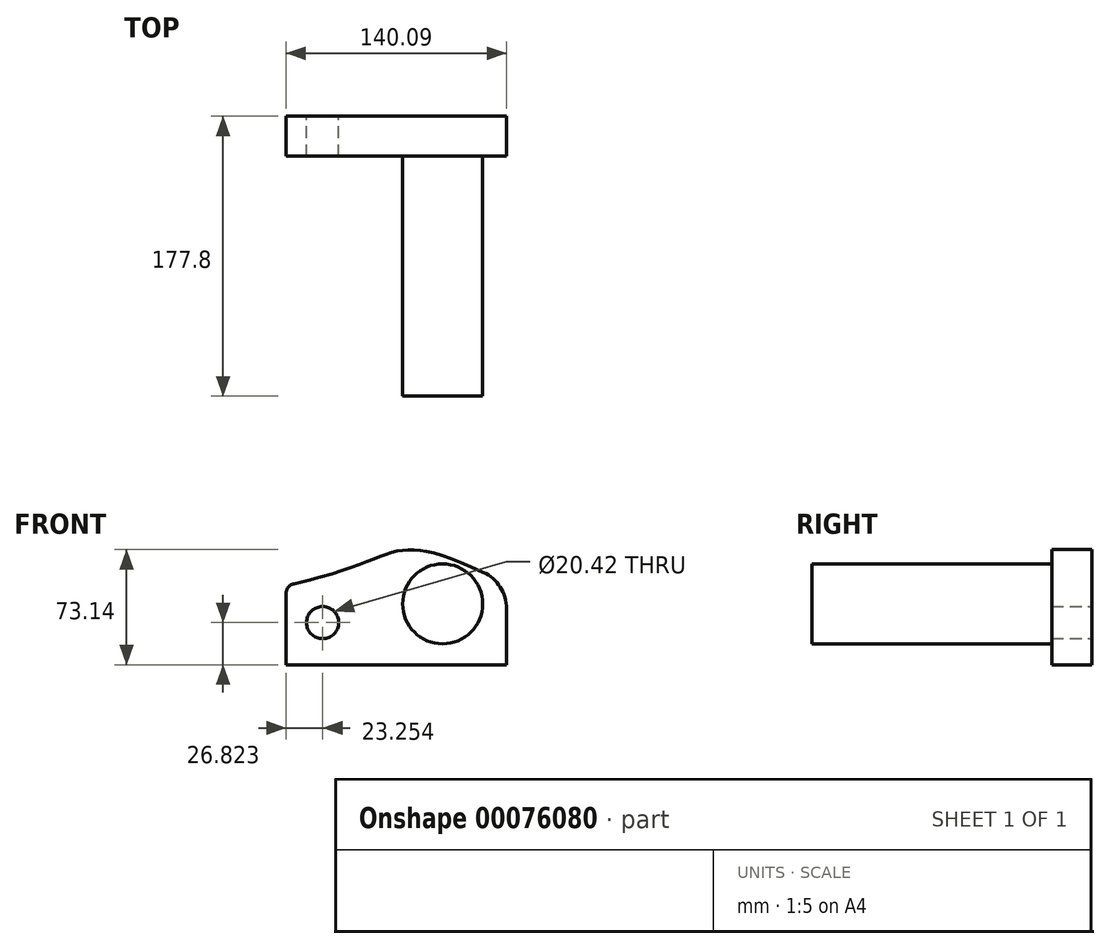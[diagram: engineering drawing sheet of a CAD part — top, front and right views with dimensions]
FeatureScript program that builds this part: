
annotation { "Feature Type Name" : "Feature", "Feature Type Description" : "" }
export const myFeature = defineFeature(function(context is Context, id is Id, definition is map)
    precondition{}
    {
        {
            var Q0;
            Q0=qCreatedBy(makeId("Front.planeOp"),FACE);
            var sketch = newSketch(context, id + "F0", { "sketchPlane" : qUnion([Q0])});
            skLineSegment(sketch, "E0", {"start": v(0, 0) * mm, "end": v(-140.09, 0) * mm});
            skLineSegment(sketch, "E1", {"start": v(-140.09, 0) * mm, "end": v(-140.09, 45.24) * mm});
            skLineSegment(sketch, "E2", {"start": v(0, 0) * mm, "end": v(0, 51.79) * mm});
            skFitSpline(sketch, "E3", {"points": [v(-140.09, 50.36) * mm, v(0, 51.79) * mm, v(40.52, 51.79) * mm], "startDerivative": vector(383.68, 80.42) * mm, "endDerivative": vector(-657.67, 513.08) * mm});
            skArc(sketch, "E4.filletArc", {"start": v(-135.12, 51.44) * mm, "mid": v(-138.7, 49.21) * mm, "end": v(-140.09, 45.24) * mm});
            skSolve(sketch);
        }
        {
            var Q0;
            Q0 = qSketchRegion(id + "F0", true);
            extrude(context, id + "F1", {"entities" : qUnion([Q0]), "depth" : 25.4 * mm});
        }
        {
            var Q0;
            Q0=makeQuery(id+"F1.opExtrude","CAP_FACE",FACE,{"disambiguationData":[OSD([sQuery(id+"F0.wireOp",EDGE,"E0"),sQuery(id+"F0.wireOp",EDGE,"E1"),sQuery(id+"F0.wireOp",EDGE,"E2"),sQuery(id+"F0.wireOp",EDGE,"E3"),sQuery(id+"F0.wireOp",EDGE,"E4.filletArc")])],"isStart":false});
            var sketch = newSketch(context, id + "F2", { "sketchPlane" : qUnion([Q0])});
            skCircle(sketch, "E5", {"center": v(-40.61, 38.69) * mm, "radius": 25.4 * mm});
            skSolve(sketch);
        }
        {
            var Q0;
            Q0 = qSketchRegion(id + "F2", true);
            extrude(context, id + "F3", {"entities" : qUnion([Q0]), "operationType" : NewBodyOperationType.ADD, "depth" : 127 * mm});
        }
        {
            var Q0;
            Q0=makeQuery(id+"F3.opExtrude","CAP_FACE",FACE,{"disambiguationData":[OSD([sQuery(id+"F2.wireOp",EDGE,"E5")])],"isStart":false});
            var sketch = newSketch(context, id + "F4", { "sketchPlane" : qUnion([Q0])});
            skLineSegment(sketch, "E6.0.0", {"start": v(-140.09, 0) * mm, "end": v(0, 0) * mm});
            skLineSegment(sketch, "E6.0.1", {"start": v(0, 0) * mm, "end": v(0, 51.79) * mm});
            skFitSpline(sketch, "E6.0.2", {"points": [v(40.52, 51.79) * mm, v(117.2, -8.03) * mm, v(-93.64, 103.09) * mm, v(-56.92, 67.8) * mm, v(-140.09, 50.36) * mm]});
            skArc(sketch, "E6.0.3", {"start": v(-135.12, 51.44) * mm, "mid": v(-138.7, 49.21) * mm, "end": v(-140.09, 45.24) * mm});
            skLineSegment(sketch, "E6.0.4", {"start": v(-140.09, 45.24) * mm, "end": v(-140.09, 0) * mm});
            skSolve(sketch);
        }
        {
            var Q0;
            Q0=makeQuery(id+"F4.imprint","IMPRINT",FACE,{"disambiguationData":[TD([[makeQuery(id+"F4.imprint","IMPRINT",EDGE,{"derivedFrom":sQuery(id+"F4.wireOp",EDGE,"E6.0.0")}),1.0]])]});
            var Q1;
            Q1=makeQuery(id+"F4.imprint","IMPRINT",FACE,{"disambiguationData":[TD([[makeQuery(id+"F4.imprint","IMPRINT",EDGE,{"derivedFrom":makeQuery(id+"F3.opExtrude","CAP_EDGE",EDGE,{"disambiguationData":[OSD([sQuery(id+"F2.wireOp",EDGE,"E5")])],"isStart":false})}),1.0]])]});
            extrude(context, id + "F5", {"entities" : qUnion([Q0, Q1]), "operationType" : NewBodyOperationType.ADD, "depth" : 25.4 * mm});
        }
        {
            var Q0;
            Q0=makeQuery(id+"F5.opExtrude","SWEPT_EDGE",EDGE,{"disambiguationData":[OSD([sQuery(id+"F4.wireOp",EDGE,"E6.0.1"),sQuery(id+"F4.wireOp",EDGE,"E6.0.2")])]});
            var Q1;
            Q1=makeQuery(id+"F1.opExtrude","SWEPT_EDGE",EDGE,{"disambiguationData":[OSD([sQuery(id+"F0.wireOp",EDGE,"E2"),sQuery(id+"F0.wireOp",EDGE,"E3")])]});
            fillet(context, id + "F6", {"entities" : qUnion([Q0, Q1]), "radius" : 25.4 * mm, "tangentPropagation" : true, "allowEdgeOverflow" : false});
        }
        {
            var Q0;
            Q0=makeQuery(id+"F1.opExtrude","CAP_FACE",FACE,{"disambiguationData":[OSD([sQuery(id+"F0.wireOp",EDGE,"E0"),sQuery(id+"F0.wireOp",EDGE,"E1"),sQuery(id+"F0.wireOp",EDGE,"E2"),sQuery(id+"F0.wireOp",EDGE,"E3"),sQuery(id+"F0.wireOp",EDGE,"E4.filletArc")])],"isStart":true});
            var sketch = newSketch(context, id + "F7", { "sketchPlane" : qUnion([Q0])});
            skCircle(sketch, "E7", {"center": v(116.84, 26.82) * mm, "radius": 10.21 * mm});
            skSolve(sketch);
        }
        {
            var Q0;
            Q0=makeQuery(id+"F7.imprint","IMPRINT",FACE,{"disambiguationData":[TD([[makeQuery(id+"F7.imprint","IMPRINT",EDGE,{"derivedFrom":sQuery(id+"F7.wireOp",EDGE,"E7")}),1.0]])]});
            extrude(context, id + "F8", {"entities" : qUnion([Q0]), "operationType" : NewBodyOperationType.REMOVE, "oppositeDirection" : true, "depth" : 211.43 * mm});
        }
    });
